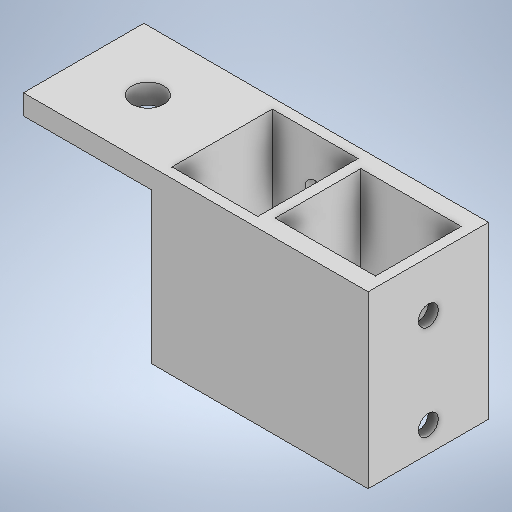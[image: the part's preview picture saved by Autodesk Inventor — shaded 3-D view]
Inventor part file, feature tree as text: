
AUTODESK INVENTOR PART (.ipt)
format: ipt  version: 2025.1 (Build 291241000, 241)  size: 258,048 bytes
history: native  units: in
note: dims shown in document units (in); Inventor stores cm internally (conversion verified against a paired STEP export)
features: extrude x5, sketch x5, direct_edit x1, move_body x1
ambient origin geometry x8: Origin, YZ Plane, XZ Plane, XY Plane, X Axis, Y Axis, Z Axis, Center Point
bodies: Solid1 (feature_tree)
feature tree (12):
  extrude  "Extrusion1"  Depth=0.625in
  extrude  "Extrusion2"  Depth=0.0625in
  extrude  "Extrusion3"  Depth=0.535in
  direct_edit  "Direct Edit1"
  extrude  "Extrusion4"  Depth=0.0625in
  extrude  "Extrusion5"  Depth=0.0625in
  sketch  "Sketch1"  dims[d0=0.535in d1=0.625in]
  sketch  "Sketch2"  dims[d2=0.045in d3=0.0625in]
  sketch  "Sketch3"  dims[d4=0.625in d5=0.535in]
  sketch  "Sketch4"  dims[d6=0.0625in d7=0.0625in]
  sketch  "Sketch5"  dims[d8=0.0625in d9=0.0625in d10=0.0625in d11=1.0in d12=0.0in d13=0.315in d14=0.125in d15=0.59in d16=0.125in d17=0.375in d18=0.0in d19=0.315in d20=0.125in d21=0.59in d22=0.125in d23=0.375in d24=0.0in d25=0.0in d26=0.0in d27=0.0625in d28=0.125in d29=0.8in d30=0.0in d31=0.2in d32=0.8in d33=0.0in]
  move_body  "Move1"
